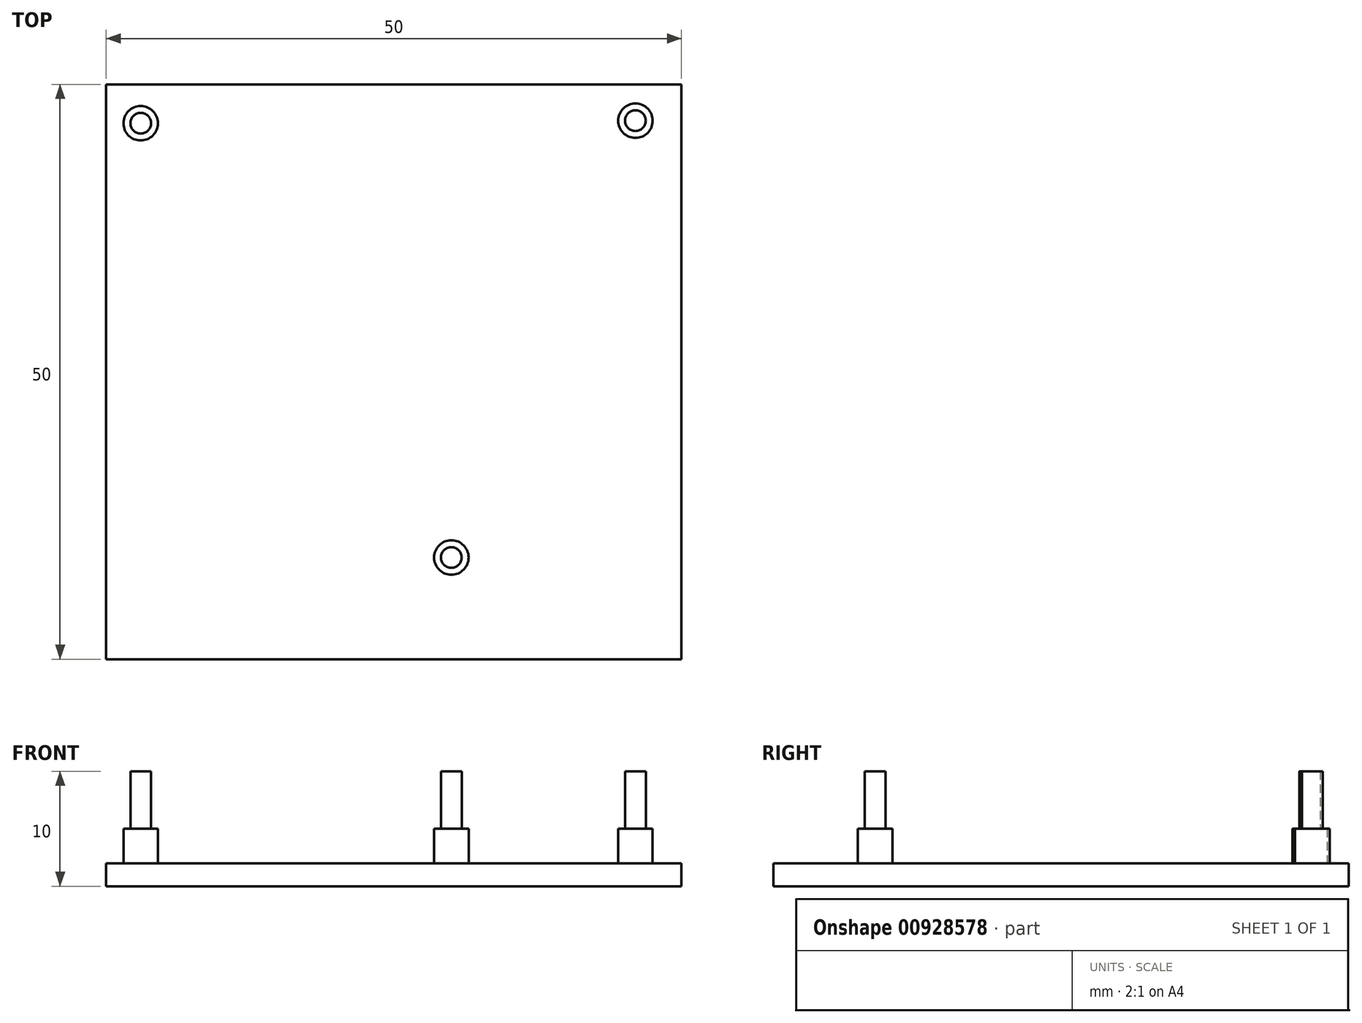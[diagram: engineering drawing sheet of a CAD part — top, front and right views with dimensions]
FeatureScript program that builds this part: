
annotation { "Feature Type Name" : "Feature", "Feature Type Description" : "" }
export const myFeature = defineFeature(function(context is Context, id is Id, definition is map)
    precondition{}
    {
        {
            var Q0;
            Q0=qCreatedBy(makeId("Top.planeOp"),FACE);
            var sketch = newSketch(context, id + "F0", { "sketchPlane" : qUnion([Q0])});
            skLineSegment(sketch, "E0.bottom", {"start": v(-25, 25) * mm, "end": v(25, 25) * mm});
            skLineSegment(sketch, "E0.top", {"start": v(-25, -25) * mm, "end": v(25, -25) * mm});
            skLineSegment(sketch, "E0.left", {"start": v(-25, 25) * mm, "end": v(-25, -25) * mm});
            skLineSegment(sketch, "E0.right", {"start": v(25, 25) * mm, "end": v(25, -25) * mm});
            skPoint(sketch, "E0.middle", {"position": v(0, 0) * mm});
            skCircle(sketch, "E1", {"center": v(-22, 21.62) * mm, "radius": 1.5 * mm});
            skCircle(sketch, "E2", {"center": v(21, 21.84) * mm, "radius": 1.5 * mm});
            skCircle(sketch, "E3", {"center": v(5, -16.16) * mm, "radius": 1.5 * mm});
            skCircle(sketch, "E4", {"center": v(-22, 21.62) * mm, "radius": 0.9 * mm});
            skCircle(sketch, "E5", {"center": v(21, 21.84) * mm, "radius": 0.9 * mm});
            skCircle(sketch, "E6", {"center": v(5, -16.16) * mm, "radius": 0.9 * mm});
            skSolve(sketch);
        }
        {
            var Q0;
            Q0=makeQuery(id+"F0.imprint","IMPRINT",FACE,{"disambiguationData":[TD([[makeQuery(id+"F0.imprint","IMPRINT",EDGE,{"derivedFrom":sQuery(id+"F0.wireOp",EDGE,"E0.bottom")}),-1.0]])]});
            extrude(context, id + "F1", {"entities" : qUnion([Q0]), "depth" : 2 * mm, "offsetDistance" : 25 * mm});
        }
        {
            var Q0;
            Q0=makeQuery(id+"F0.imprint","IMPRINT",FACE,{"disambiguationData":[TD([[makeQuery(id+"F0.imprint","IMPRINT",EDGE,{"derivedFrom":sQuery(id+"F0.wireOp",EDGE,"E1")}),1.0]])]});
            var Q1;
            Q1=makeQuery(id+"F0.imprint","IMPRINT",FACE,{"disambiguationData":[TD([[makeQuery(id+"F0.imprint","IMPRINT",EDGE,{"derivedFrom":sQuery(id+"F0.wireOp",EDGE,"E2")}),1.0]])]});
            var Q2;
            Q2=makeQuery(id+"F0.imprint","IMPRINT",FACE,{"disambiguationData":[TD([[makeQuery(id+"F0.imprint","IMPRINT",EDGE,{"derivedFrom":sQuery(id+"F0.wireOp",EDGE,"E3")}),1.0]])]});
            extrude(context, id + "F2", {"entities" : qUnion([Q0, Q1, Q2]), "operationType" : NewBodyOperationType.ADD, "depth" : 5 * mm, "offsetDistance" : 25 * mm});
        }
        {
            var Q0;
            Q0=makeQuery(id+"F0.imprint","IMPRINT",FACE,{"disambiguationData":[TD([[makeQuery(id+"F0.imprint","IMPRINT",EDGE,{"derivedFrom":sQuery(id+"F0.wireOp",EDGE,"E4")}),1.0]])]});
            var Q1;
            Q1=makeQuery(id+"F0.imprint","IMPRINT",FACE,{"disambiguationData":[TD([[makeQuery(id+"F0.imprint","IMPRINT",EDGE,{"derivedFrom":sQuery(id+"F0.wireOp",EDGE,"E5")}),1.0]])]});
            var Q2;
            Q2=makeQuery(id+"F0.imprint","IMPRINT",FACE,{"disambiguationData":[TD([[makeQuery(id+"F0.imprint","IMPRINT",EDGE,{"derivedFrom":sQuery(id+"F0.wireOp",EDGE,"E6")}),1.0]])]});
            extrude(context, id + "F3", {"entities" : qUnion([Q0, Q1, Q2]), "operationType" : NewBodyOperationType.ADD, "depth" : 10 * mm, "offsetDistance" : 25 * mm});
        }
    });
